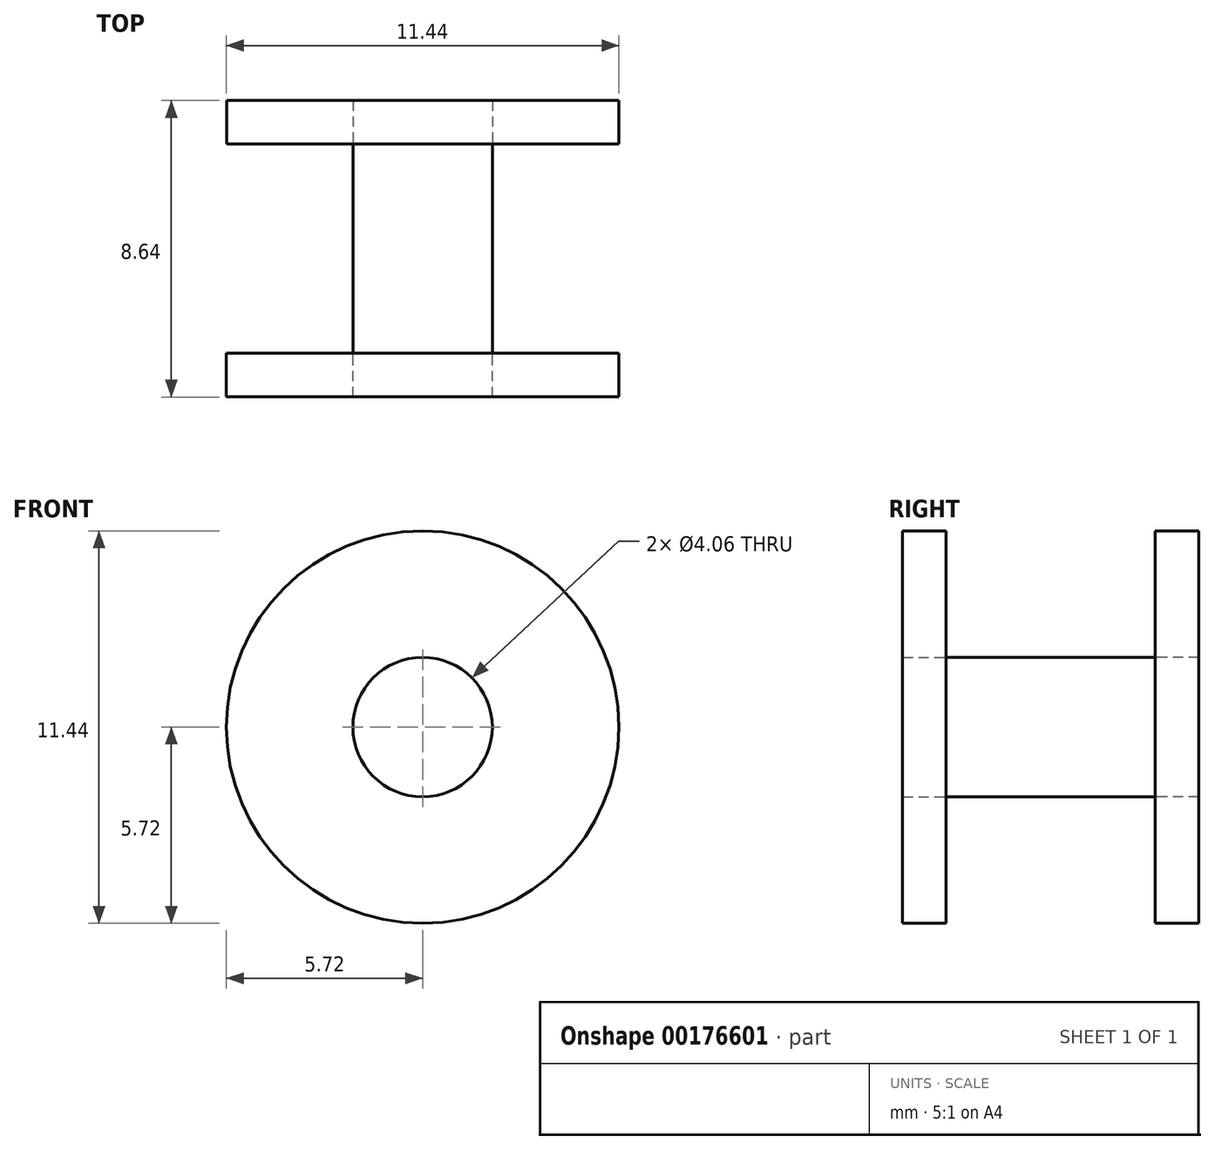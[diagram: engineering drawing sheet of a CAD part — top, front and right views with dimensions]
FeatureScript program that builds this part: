
annotation { "Feature Type Name" : "Feature", "Feature Type Description" : "" }
export const myFeature = defineFeature(function(context is Context, id is Id, definition is map)
    precondition{}
    {
        {
            var Q0;
            Q0=qCreatedBy(makeId("Front.planeOp"),FACE);
            var sketch = newSketch(context, id + "F0", { "sketchPlane" : qUnion([Q0])});
            skCircle(sketch, "E0", {"center": v(0, 0) * mm, "radius": 2.03 * mm});
            skSolve(sketch);
        }
        {
            var Q0;
            Q0=makeQuery(id+"F0.imprint","IMPRINT",FACE,{"disambiguationData":[TD([[makeQuery(id+"F0.imprint","IMPRINT",EDGE,{"derivedFrom":sQuery(id+"F0.wireOp",EDGE,"E0")}),1.0]])]});
            extrude(context, id + "F1", {"entities" : qUnion([Q0]), "depth" : 3.05 * mm});
        }
        {
            var Q0;
            Q0=makeQuery(id+"F1.opExtrude","CAP_FACE",FACE,{"disambiguationData":[OSD([sQuery(id+"F0.wireOp",EDGE,"E0")])],"isStart":true});
            extrude(context, id + "F2", {"entities" : qUnion([Q0]), "operationType" : NewBodyOperationType.ADD, "depth" : 3.05 * mm});
        }
        {
            var Q0;
            Q0=makeQuery(id+"F2.opExtrude","CAP_FACE",FACE,{"disambiguationData":[OSD([sQuery(id+"F0.wireOp",EDGE,"E0")])],"isStart":false});
            var sketch = newSketch(context, id + "F3", { "sketchPlane" : qUnion([Q0])});
            skCircle(sketch, "E1", {"center": v(0, 0) * mm, "radius": 5.71 * mm});
            skSolve(sketch);
        }
        {
            var Q0;
            Q0=makeQuery(id+"F3.imprint","IMPRINT",FACE,{"disambiguationData":[TD([[makeQuery(id+"F3.imprint","IMPRINT",EDGE,{"derivedFrom":sQuery(id+"F3.wireOp",EDGE,"E1")}),1.0]])]});
            extrude(context, id + "F4", {"entities" : qUnion([Q0]), "depth" : 1.27 * mm});
        }
        {
            var Q0;
            Q0=makeQuery(id+"F1.opExtrude","CAP_FACE",FACE,{"disambiguationData":[OSD([sQuery(id+"F0.wireOp",EDGE,"E0")])],"isStart":false});
            var sketch = newSketch(context, id + "F5", { "sketchPlane" : qUnion([Q0])});
            skCircle(sketch, "E2", {"center": v(0, 0) * mm, "radius": 5.72 * mm});
            skSolve(sketch);
        }
        {
            var Q0;
            Q0=makeQuery(id+"F5.imprint","IMPRINT",FACE,{"disambiguationData":[TD([[makeQuery(id+"F5.imprint","IMPRINT",EDGE,{"derivedFrom":sQuery(id+"F5.wireOp",EDGE,"E2")}),1.0]])]});
            extrude(context, id + "F6", {"entities" : qUnion([Q0]), "depth" : 1.27 * mm});
        }
        {
            var Q0;
            Q0=makeQuery(id+"F2.opExtrude","CAP_FACE",FACE,{"disambiguationData":[OSD([sQuery(id+"F0.wireOp",EDGE,"E0")])],"isStart":false});
            extrude(context, id + "F7", {"entities" : qUnion([Q0]), "depth" : 1.27 * mm});
        }
        {
            var Q0;
            Q0=makeQuery(id+"F1.opExtrude","CAP_FACE",FACE,{"disambiguationData":[OSD([sQuery(id+"F0.wireOp",EDGE,"E0")])],"isStart":false});
            extrude(context, id + "F8", {"entities" : qUnion([Q0]), "depth" : 1.27 * mm});
        }
    });
